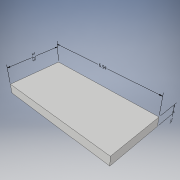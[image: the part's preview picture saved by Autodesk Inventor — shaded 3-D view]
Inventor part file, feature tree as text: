
AUTODESK INVENTOR PART (.ipt)
format: ipt  version: 2019 (Build 230136000, 136)  size: 101,888 bytes
history: native  units: in
note: dims shown in document units (in); Inventor stores cm internally (conversion verified against a paired STEP export)
features: other x4, extrude x1, sketch x1
ambient origin geometry x8: Origin, YZ Plane, XZ Plane, XY Plane, X Axis, Y Axis, Z Axis, Center Point
bodies: Solid1 (feature_tree)
feature tree (6):
  other  "Annotations"
  extrude  "Extrusion1"  Depth=3.25in
  sketch  "Sketch1"  dims[d0=6.9375in d1=3.25in d2=0.5625in d3=0.0in d10=0.0in d11=0.3937in d12=3.25in d4=0.0in d5=0.3937in d6=6.9375in d7=0.0in d8=0.3937in d9=0.5625in]
  other  "Linear Dimension 1"
  other  "Linear Dimension 2"
  other  "Linear Dimension 3"
